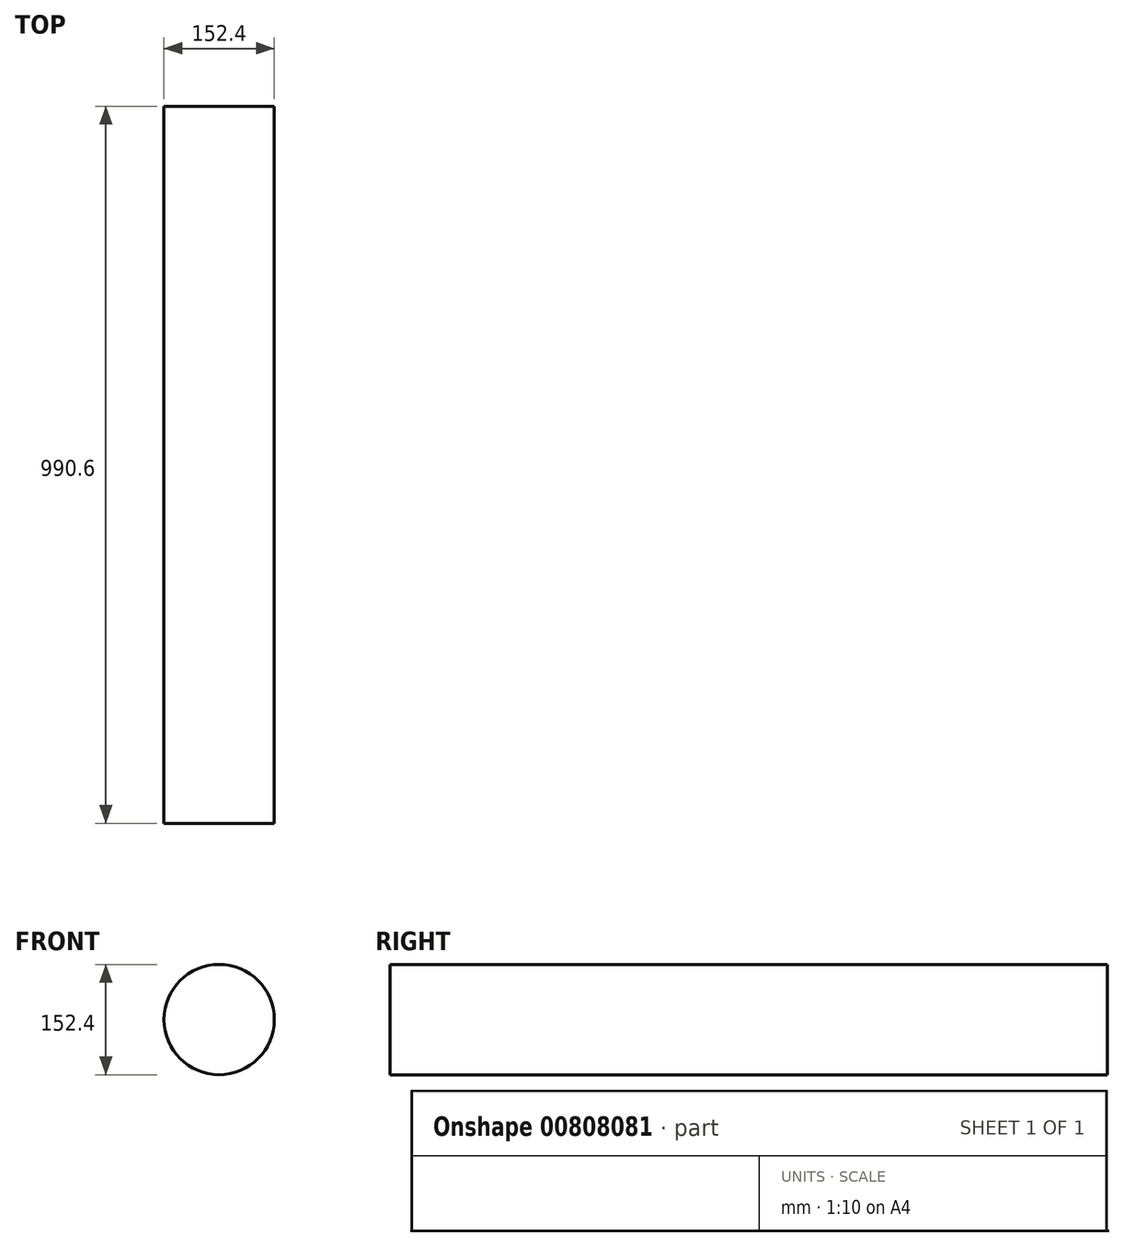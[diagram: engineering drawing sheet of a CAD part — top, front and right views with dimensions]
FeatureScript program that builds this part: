
annotation { "Feature Type Name" : "Feature", "Feature Type Description" : "" }
export const myFeature = defineFeature(function(context is Context, id is Id, definition is map)
    precondition{}
    {
        {
            var Q0;
            Q0=qCreatedBy(makeId("Front.planeOp"),FACE);
            var sketch = newSketch(context, id + "F0", { "sketchPlane" : qUnion([Q0])});
            skCircle(sketch, "E0", {"center": v(0, 0) * mm, "radius": 76.2 * mm});
            skSolve(sketch);
        }
        {
            var Q0;
            Q0 = qSketchRegion(id + "F0", true);
            extrude(context, id + "F1", {"entities" : qUnion([Q0]), "depth" : 990.6 * mm, "offsetDistance" : 25.4 * mm});
        }
    });
